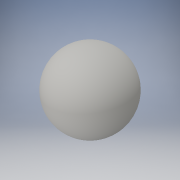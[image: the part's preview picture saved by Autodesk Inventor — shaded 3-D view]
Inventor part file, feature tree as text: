
AUTODESK INVENTOR PART (.ipt)
format: ipt  version: 2016 (Build 200138000, 138)  size: 115,200 bytes
history: native  units: in
note: dims shown in document units (in); Inventor stores cm internally (conversion verified against a paired STEP export)
features: revolve x1, sketch x1
ambient origin geometry x8: Origin, YZ Plane, XZ Plane, XY Plane, X Axis, Y Axis, Z Axis, Center Point
bodies: Solid1 (feature_tree)
feature tree (2):
  revolve  "Revolution1"  [1 undecoded]
  sketch  "Sketch1"  dims[d0=11.1408in d1=5.5704in d2=90.0deg]
note: 1 required parameter value undecoded (feature->parameter linkage not recoverable at this tier; creation-order binding heuristic only, values carry confidence <= 0.55)
